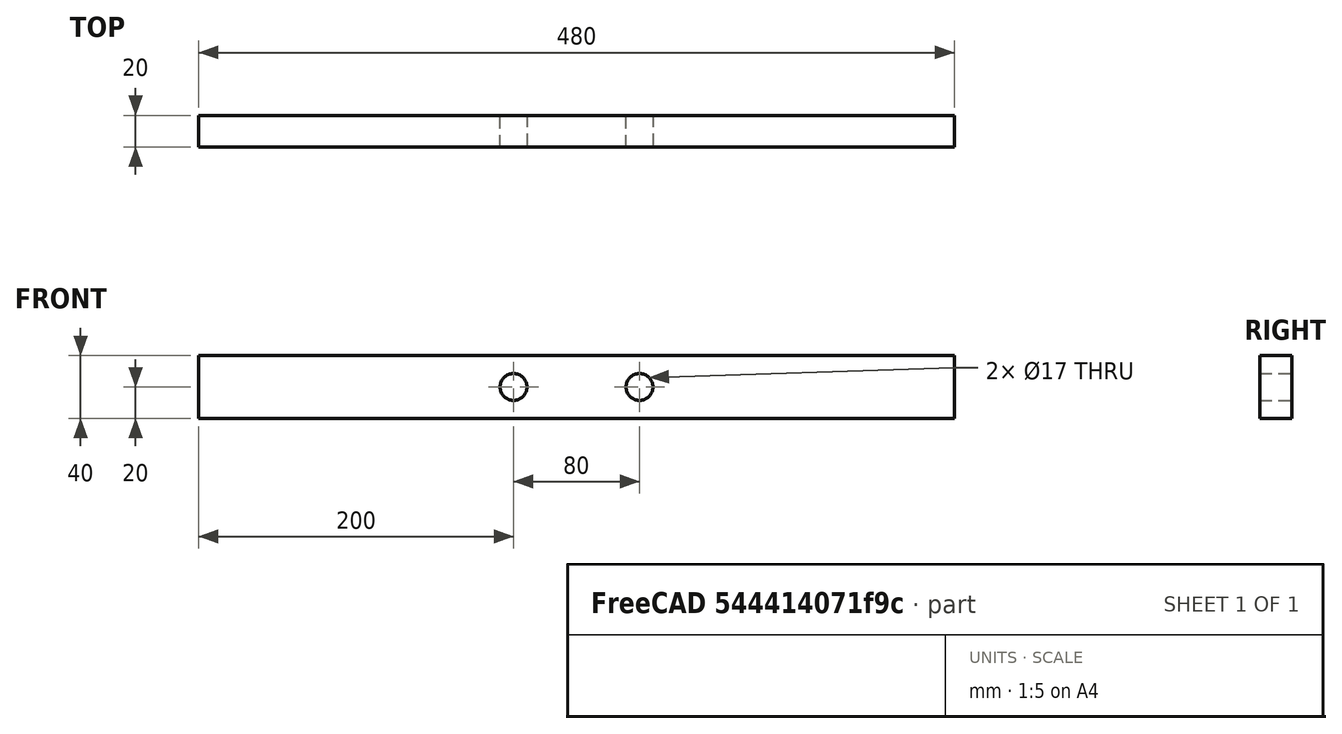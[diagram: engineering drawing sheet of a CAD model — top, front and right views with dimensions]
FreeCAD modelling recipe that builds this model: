
FCSTD DOCUMENT  (FreeCAD 0.19R24366 (Git))
Label: Part5Hollow
License: All rights reserved
LicenseURL: http://en.wikipedia.org/wiki/All_rights_reserved
objects: TechDraw::DrawViewDimension×2, Sketcher::SketchObject×1, PartDesign::Pad×1, PartDesign::Body×1, TechDraw::DrawSVGTemplate×1, TechDraw::DrawViewPart×1, TechDraw::DrawPage×1
note: 4 computed .brp shape members not serialized (recipe doc carries the construction recipe); baked Part::Feature solids carry a one-line shape summary decoded from their .brp

FEATURE [Sketcher::SketchObject] Sketch
  FullyConstrained = true
  MapMode = 5
  Placement = pos=(0,0,0) rot=(1,0,0;1.5708rad)
  Support = -> [XZ_Plane]
  sketch-geometry (6):
    g0: LineSegment StartX=-240 StartY=20 StartZ=0 EndX=240 EndY=20 EndZ=0
    g1: LineSegment StartX=240 StartY=20 StartZ=0 EndX=240 EndY=-20 EndZ=0
    g2: LineSegment StartX=240 StartY=-20 StartZ=0 EndX=-240 EndY=-20 EndZ=0
    g3: LineSegment StartX=-240 StartY=-20 StartZ=0 EndX=-240 EndY=20 EndZ=0
    g4: Circle CenterX=-40 CenterY=1.8e-15 CenterZ=0 NormalX=0 NormalY=0 NormalZ=1 AngleXU=0 Radius=8.5
    g5: Circle CenterX=40 CenterY=-4e-16 CenterZ=0 NormalX=0 NormalY=0 NormalZ=1 AngleXU=0 Radius=8.5
  constraints (18):
    c: Coincident(g0,g1)
    c: Coincident(g1,g2)
    c: Coincident(g2,g3)
    c: Coincident(g3,g0)
    c: Horizontal(g0)
    c: Horizontal(g2)
    c: Vertical(g1)
    c: Vertical(g3)
    c: DistanceX(g0,g0) = 480
    c: DistanceY(g3,g3) = 40
    c: DistanceX(g2,g-1) = 240
    c: DistanceY(g-1,g0) = 20
    c: Diameter(g4) = 17
    c: DistanceX(g2,g4) = 200
    c: DistanceY(g4,g0) = 20
    c: Equal(g4,g5) = 17
    c: DistanceX(g5,g1) = 200
    c: DistanceY(g5,g0) = 20
FEATURE [PartDesign::Pad] Pad
  Direction = (1,1,1)
  Length = 20
  Length2 = 100
  Placement = pos=(0,0,0) rot=(1,0,0;1.5708rad)
  Profile = -> Sketch
  Type = 0
FEATURE [PartDesign::Body] Body
  Group = -> [Sketch,Pad]
  Origin = -> Origin
  Tip = -> Pad
FEATURE [TechDraw::DrawSVGTemplate] Template
  EditableTexts = AUTHOR_NAME=Natan Hari Pamungkas; DN=Part - 05; DRAWING_TITLE=Part Besi Hollow - 05; FC-DATE=18/03/2022; FC-REV=REV A; FC-SC=0.5; FC-SH=X / Y; FC-SI=A4; FreeCAD_DRAWING=Ketebalan menyesuaikan, lubang jangan dibuat dulu; PN=Hollow - 05; SI-1=Besi Hollow Ukuran 2 cm x 4 cm; SI-3=Jumlah item 1
  Height = 210
  Orientation = 1
  Width = 297
FEATURE [TechDraw::DrawViewPart] View  label="Front"
  CoarseView = false
  Direction = (0,-1,0)
  Focus = 100
  HardHidden = false
  IsoCount = 0
  IsoHidden = false
  IsoVisible = false
  LockPosition = false
  Perspective = false
  Rotation = 0
  Scale = 0.5
  ScaleType = 0
  SeamHidden = false
  SeamVisible = true
  SmoothHidden = false
  SmoothVisible = true
  Source = -> [Body]
  X = 151.381
  XDirection = (1,0,0)
  Y = 129.508
FEATURE [TechDraw::DrawViewDimension] Dimension
  Arbitrary = false
  ArbitraryTolerances = false
  EqualTolerance = true
  FormatSpec = %.2f
  FormatSpecOverTolerance = %+.2f
  FormatSpecUnderTolerance = %+.2f
  Inverted = false
  LockPosition = false
  MeasureType = 1
  OverTolerance = 0
  References2D = -> [View]
  Rotation = 0
  ScaleType = 0
  TheoreticalExact = false
  Type = 1
  UnderTolerance = 0
  X = -4.81029
  Y = 30.7602
FEATURE [TechDraw::DrawViewDimension] Dimension001
  Arbitrary = false
  ArbitraryTolerances = false
  EqualTolerance = true
  FormatSpec = %.2f
  FormatSpecOverTolerance = %+.2f
  FormatSpecUnderTolerance = %+.2f
  Inverted = false
  LockPosition = false
  MeasureType = 1
  OverTolerance = 0
  References2D = -> [View]
  Rotation = 0
  ScaleType = 0
  TheoreticalExact = false
  Type = 2
  UnderTolerance = 0
  X = -126.583
  Y = -0.253173
FEATURE [TechDraw::DrawPage] Page
  KeepUpdated = true
  NextBalloonIndex = 1
  ProjectionType = 0
  Template = -> Template
  Views = -> [View,Dimension,Dimension001]
